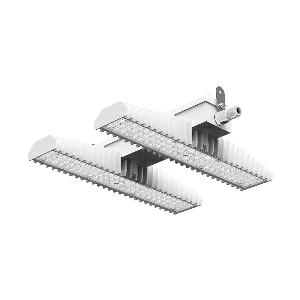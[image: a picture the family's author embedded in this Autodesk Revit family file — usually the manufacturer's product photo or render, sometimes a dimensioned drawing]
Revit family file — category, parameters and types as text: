
# Revit family: 3f_filippi_-_3f_lem_ht_concentrato_3f_filippi_-_59032_-_3f_lem_2_ht_led_60_cr_conc
name_source: partatom
category: Lighting Fixtures
units: mm (PartAtom-declared; Revit-internal decimal feet)

## family parameters
Cut with Voids When Loaded = No
Host = Face
Light Source = No
Part Type = Normal
Room Calculation Point = No
Round Connector Dimension = Use Diameter
Shared = No

## types (1)
- 3F Filippi - 3F LEM HT Concentrato (1 x LED, 10419 lm, 68 W, 4000 K)
    Apparent Load = 68 VA
    Approval mark = ENEC
    CIE Flux Codes = 83 96 99 100 100
    Color Rendering = 80
    Color Temperature = 4000 K
    Control Gear = Electronic ballast
    Default Elevation = 1800 mm
    Description = Industrial luminaire with high light output and high luminous efficiency designed with the most innovative technologies for environments with temperature up to 70°C.

ILLUMINOTECHNICAL
Luminous efficiency 100% (DLOR 100%, ULOR 0%).
Initial luminous flux of the luminaire 10419 lm.
Direct symmetric narrow distribution: the illuminated area has a elliptical shape.
Installation Interdistance Transv.D = 0.52 x hu - Long.D = 1.16 x hu.
Tabular UGR (CIE 117 - 4H-8H; S=0.25H; 70/50/20): RUG 15.3 - 19.
Beam angle: 31° - 73°.
Luminous efficacy 153 lm/W.
Lifetime (L93/B10): 30000 h. (tq+25°C)
Lifetime (L90/B10): 50000 h. (tq+25°C)
Lifetime (L85/B10): 80000 h. (tq+25°C)
Lifetime (L80/B10): 100000 h. (tq+25°C)
Lifetime (L85/B10): 50000 h. (tq+70°C)
Sudden decreased luminous flux after 50000 hours: 0% (C0).
Photobiological safety in compliance with IEC/TR 62778: RG0 risk exempt, (IEC 62471).
In compliance with IEC/EN 62722-2-1 - IEC/EN 62717 standards.
Luminous flux at +70°C: -13.5%.

SOURCE
2 Mid-Power linear LED modules 30W/840.
Energy efficiency class (UE 2019/2020 - UE 2019/2015): C.
CIE 13.3 Colour rendering index: CRI >80 (R9 <50%).
IES TM-30 Fidelity Index: Rf = 84 Rg = 95.
CCT nominal colour temperature 4000 K.
Colour initial tolerance (MacAdam): SDCM 3.

MECHANICAL
Passive modular heatsinks in die-casted aluminium, painted in white colour.
To optimize the thermal management of the LED module, the heatsinks are oversized and provided with self-cleaning of cooling fins.
Wiring body in aluminium and galvanised steel anchored solidly to the sinks and thermally separated.
3F Lens lenses with high luminous efficiency, transparent polycarbonate, fixed to the LED modules.
Fixing brackets in stainless steel.
Luminaire with limited surface temperature. - D - (EN 60598-2-24)
Dimensions: 470x542 mm, height 129 mm. Weight 9.265 kg.
IP65 protection degree.
Mechanical strength to impacts IK08 (5 joule).
Glow-wire test resistance 850°C.

ELECTRICAL
Halogen Free electronic wiring 230V-50/60Hz, power factor 0.95, THD <25%, constant output current, class I, 1 driver.
Power of the luminaire 68 W.
CE - IEC 60598-1 - EN 60598-1.
SAFE FLICKER: PstLM=<1 and SVM=<0.4 (IEC TR 61547-1 and IEC TR 63158), to ensure a more comfortable and safe light.
Luminaire compliant with EN 60598-2-22 for power supply from a centralised emergency system CPSS (Central Power Supply System), not incorporated in the luminaire - high risk areas excluded. The default power and flux are 100% in AC and 100% in DC.
Ambient temperature from -30°C to +70°C.
Temperature class T6 max 85°C.
Quick connection via M20 3P connector with 9-13 mm tightening range.
Power unit positioned on a separate compartment by the LED module to ensure optimum temperatures of cabling components, to be inspectable and maintainable.
Relative humidity UR: <85%.

INSTALLATION
Ceiling / Suspended / Wall.
All accessories dedicated to this product are available on the Catalog and on our website www.3F-Filippi.com.

APPLICATIONS
In commercial environments, exhibition and industrial areas, stores, open areas.
Applications with high ambient temperature up to 70°C.

WARNING
Fixture not suitable for cold stores with an ambient temperature <0°C and/or relative humidity >85%.
Luminaire designed for disposal/recycling at end-of-life.
Replaceable (LED only) light source by a professional. Replaceable control gear by a professional.
    Height = 129 mm
    Lamp = 1 x LED
    Lamp Light Flux = 10419 lm
    Lamp Power = 68 W
    Lamp count = 1
    Length = 470 mm
    Lifetime = 50000 h
    Luminous efficacy = 153 lm/W
    Manufacturer = 3F Filippi
    ModVariant = No
    Model = 3F Filippi - 59032 - 3F LEM 2 HT LED 60 CR CONC
    Mounting Place = Ceiling
    Mounting Type = Pendant
    Number of Poles = 1
    OnlyDefault = Yes
    Power Factor = 1
    Product Name = 3F Filippi - 3F LEM HT Concentrato
    Product group = pendant luminaire
    ProductGroupID = 9
    Protection Class = Protection class I
    Protection Degree = IP 65
    RLX_Detail_Level = 1
    RLX_Emergency_Light_Flux = 0 lm
    RLX_Emergency_Type = 0
    RLX_Emergency_Type_DB = No
    RlxData = <blob elided: 95797 chars, md5=4df1ea80>
    Socket = socket
    Standby Power = 0 W
    System Light Flux = 10419 lm
    System Power = 68 W
    Type Comments = Product without accessories
    Type Image = 3f_filippi_-_lem_2.jpg
    URL = http://relux.com
    VarID = ---
    Voltage = 0 V
    Weight = 0.00 kg
    Width = 542 mm

## geometry (parser evidence)
native form markers: Blend x4, Sweep x13
no freeform markers — native parametric forms only
